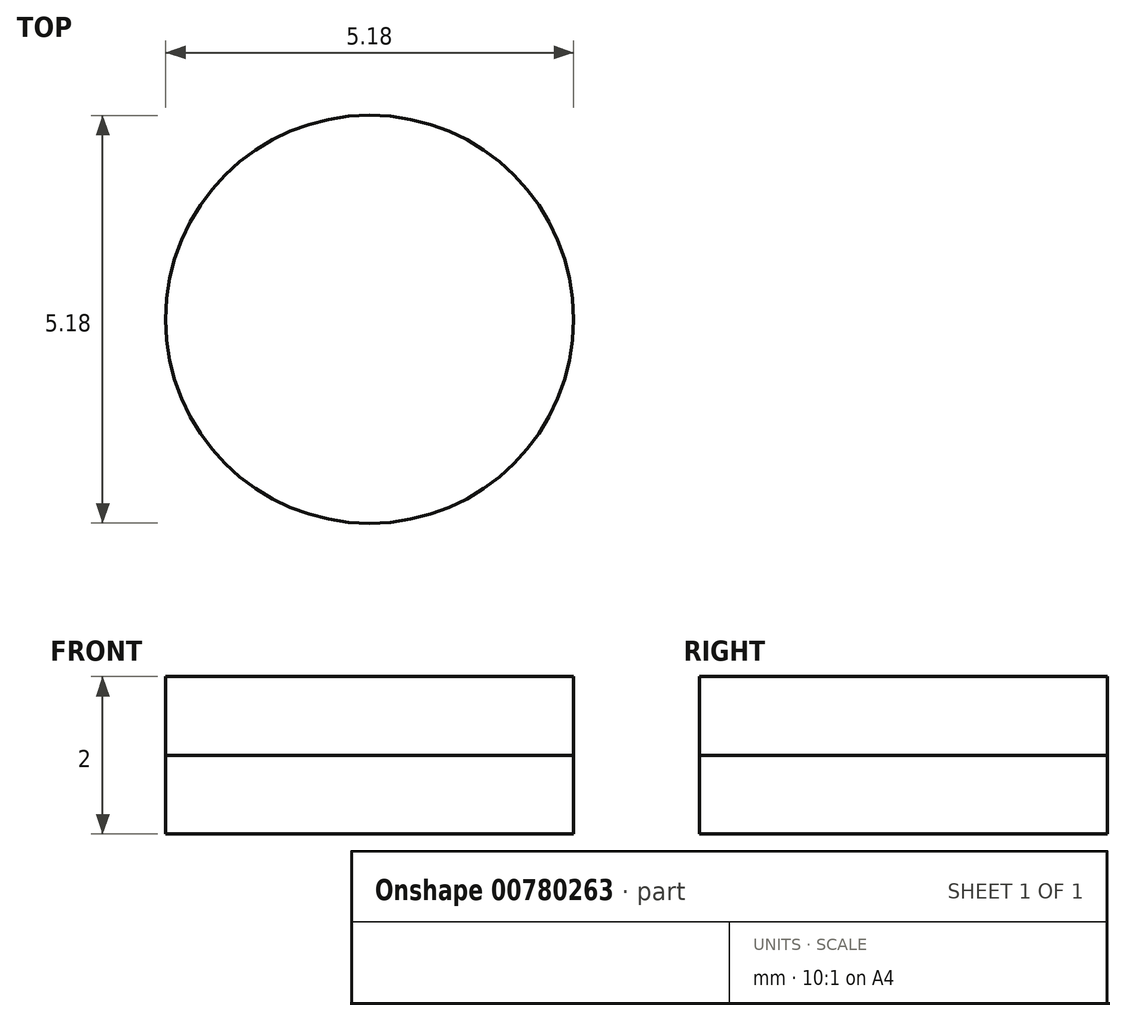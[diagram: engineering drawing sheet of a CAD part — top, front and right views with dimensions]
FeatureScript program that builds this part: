
annotation { "Feature Type Name" : "Feature", "Feature Type Description" : "" }
export const myFeature = defineFeature(function(context is Context, id is Id, definition is map)
    precondition{}
    {
        {
            var Q0;
            Q0=qCreatedBy(makeId("Top.planeOp"),FACE);
            var sketch = newSketch(context, id + "F0", { "sketchPlane" : qUnion([Q0])});
            skCircle(sketch, "E0", {"center": v(0, 0) * mm, "radius": 2.6 * mm});
            skSolve(sketch);
        }
        {
            var Q0;
            Q0 = qSketchRegion(id + "F0", true);
            extrude(context, id + "F1", {"entities" : qUnion([Q0]), "depth" : 1 * mm, "offsetDistance" : 25 * mm});
        }
        {
            var Q0;
            Q0=makeQuery(id+"F1.opExtrude","CAP_FACE",FACE,{"disambiguationData":[OSD([sQuery(id+"F0.wireOp",EDGE,"E0")])],"isStart":false});
            extrude(context, id + "F2", {"entities" : qUnion([Q0]), "depth" : 1 * mm, "offsetDistance" : 25 * mm});
        }
    });
